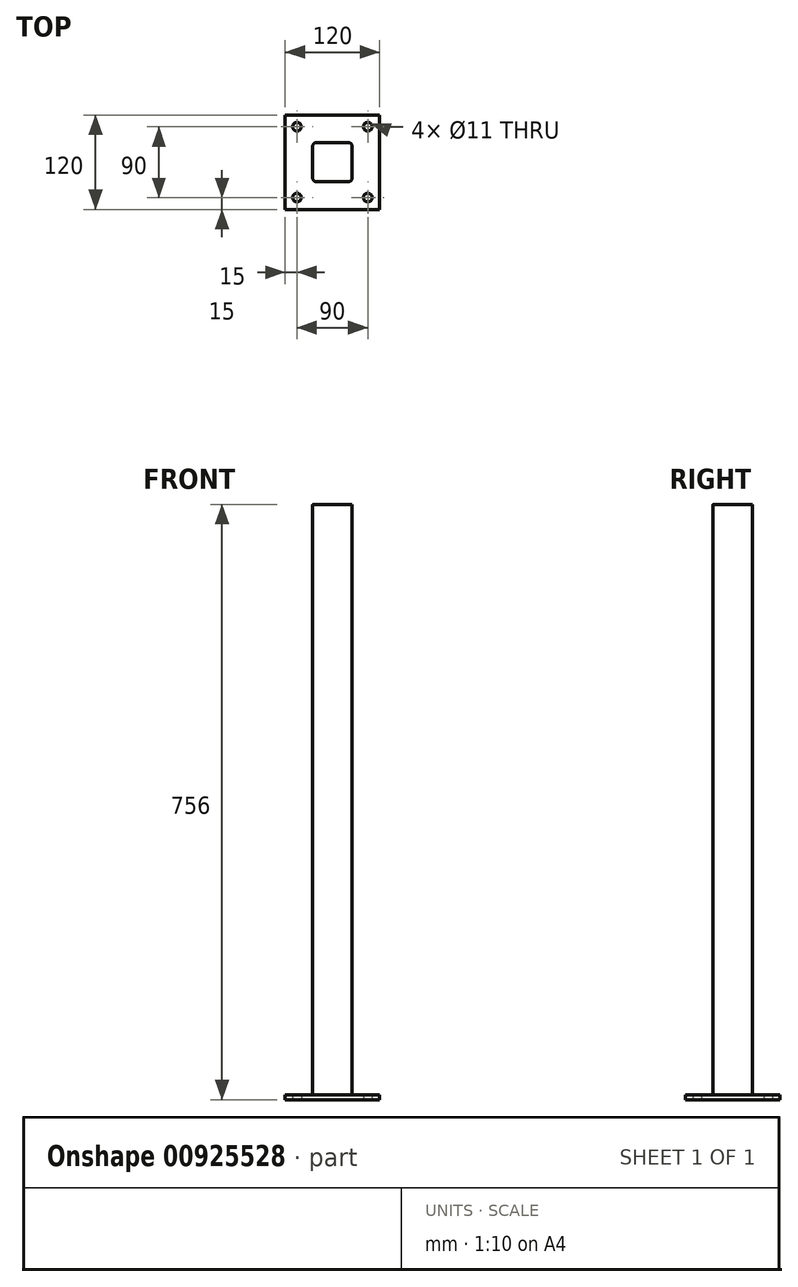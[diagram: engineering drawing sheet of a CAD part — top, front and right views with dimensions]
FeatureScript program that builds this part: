
annotation { "Feature Type Name" : "Feature", "Feature Type Description" : "" }
export const myFeature = defineFeature(function(context is Context, id is Id, definition is map)
    precondition{}
    {
        {
            var Q0;
            Q0=qCreatedBy(makeId("Top.planeOp"),FACE);
            var sketch = newSketch(context, id + "F0", { "sketchPlane" : qUnion([Q0])});
            skLineSegment(sketch, "E0.bottom", {"start": v(60, -60) * mm, "end": v(-60, -60) * mm});
            skLineSegment(sketch, "E0.top", {"start": v(60, 60) * mm, "end": v(-60, 60) * mm});
            skLineSegment(sketch, "E0.left", {"start": v(60, -60) * mm, "end": v(60, 60) * mm});
            skLineSegment(sketch, "E0.right", {"start": v(-60, -60) * mm, "end": v(-60, 60) * mm});
            skPoint(sketch, "E0.middle", {"position": v(0, 0) * mm});
            skLineSegment(sketch, "E1", {"start": v(-60, -60) * mm, "end": v(60, 60) * mm, "construction": true});
            skCircle(sketch, "E2", {"center": v(-45, -45) * mm, "radius": 5.5 * mm});
            skCircle(sketch, "E3.1.0", {"center": v(45, -45) * mm, "radius": 5.5 * mm});
            skCircle(sketch, "E3.2.0", {"center": v(45, 45) * mm, "radius": 5.5 * mm});
            skCircle(sketch, "E3.3.0", {"center": v(-45, 45) * mm, "radius": 5.5 * mm});
            skSolve(sketch);
        }
        {
            var Q0;
            Q0=makeQuery(id+"F0.imprint","IMPRINT",FACE,{"disambiguationData":[TD([[makeQuery(id+"F0.imprint","IMPRINT",EDGE,{"derivedFrom":sQuery(id+"F0.wireOp",EDGE,"E0.bottom")}),-1.0]])]});
            var Q1;
            Q1=makeQuery(id+"F0.imprint","IMPRINT",FACE,{"disambiguationData":[TD([[makeQuery(id+"F0.imprint","IMPRINT",EDGE,{"derivedFrom":sQuery(id+"F0.wireOp",EDGE,"173swOtm-QqvV-jqn0-FXP9-fX69LT3HRAmF.bottom")}),-1.0]])]});
            extrude(context, id + "F1", {"entities" : qUnion([Q0, Q1]), "depth" : 6 * mm, "offsetDistance" : 25 * mm});
        }
        {
            var Q0;
            Q0=makeQuery(id+"F1.opExtrude","CAP_FACE",FACE,{"disambiguationData":[OSD([sQuery(id+"F0.wireOp",EDGE,"E0.bottom"),sQuery(id+"F0.wireOp",EDGE,"E0.top"),sQuery(id+"F0.wireOp",EDGE,"E0.left"),sQuery(id+"F0.wireOp",EDGE,"E0.right"),sQuery(id+"F0.wireOp",EDGE,"E2"),sQuery(id+"F0.wireOp",EDGE,"E3.1.0"),sQuery(id+"F0.wireOp",EDGE,"E3.2.0"),sQuery(id+"F0.wireOp",EDGE,"E3.3.0")])],"isStart":false});
            var sketch = newSketch(context, id + "F2", { "sketchPlane" : qUnion([Q0])});
            skLineSegment(sketch, "E4.bottom", {"start": v(25, -25) * mm, "end": v(-25, -25) * mm});
            skLineSegment(sketch, "E4.top", {"start": v(25, 25) * mm, "end": v(-25, 25) * mm});
            skLineSegment(sketch, "E4.left", {"start": v(25, -25) * mm, "end": v(25, 25) * mm});
            skLineSegment(sketch, "E4.right", {"start": v(-25, -25) * mm, "end": v(-25, 25) * mm});
            skPoint(sketch, "E4.middle", {"position": v(0, 0) * mm});
            skSolve(sketch);
        }
        {
            var Q0;
            Q0=makeQuery(id+"F2.imprint","IMPRINT",FACE,{"disambiguationData":[TD([[makeQuery(id+"F2.imprint","IMPRINT",EDGE,{"derivedFrom":sQuery(id+"F2.wireOp",EDGE,"E4.bottom")}),-1.0]])]});
            extrude(context, id + "F3", {"entities" : qUnion([Q0]), "operationType" : NewBodyOperationType.ADD, "depth" : 750 * mm, "offsetDistance" : 25 * mm});
        }
        {
            var Q0;
            Q0=makeQuery(id+"F3.opExtrude","SWEPT_EDGE",EDGE,{"disambiguationData":[OSD([sQuery(id+"F2.wireOp",EDGE,"E4.bottom"),sQuery(id+"F2.wireOp",EDGE,"E4.right")])]});
            var Q1;
            Q1=makeQuery(id+"F3.opExtrude","SWEPT_EDGE",EDGE,{"disambiguationData":[OSD([sQuery(id+"F2.wireOp",EDGE,"E4.bottom"),sQuery(id+"F2.wireOp",EDGE,"E4.left")])]});
            var Q2;
            Q2=makeQuery(id+"F3.opExtrude","SWEPT_EDGE",EDGE,{"disambiguationData":[OSD([sQuery(id+"F2.wireOp",EDGE,"E4.top"),sQuery(id+"F2.wireOp",EDGE,"E4.left")])]});
            var Q3;
            Q3=makeQuery(id+"F3.opExtrude","SWEPT_EDGE",EDGE,{"disambiguationData":[OSD([sQuery(id+"F2.wireOp",EDGE,"E4.top"),sQuery(id+"F2.wireOp",EDGE,"E4.right")])]});
            fillet(context, id + "F4", {"entities" : qUnion([Q0, Q1, Q2, Q3]), "radius" : 5 * mm, "tangentPropagation" : true, "allowEdgeOverflow" : false});
        }
    });
